# Revit family: Modelo mais complexo
name_source: partatom
category: Portas
revit_build: Autodesk Revit Architecture 2015 (Build: 20140606_1530(x64)
units: mm (PartAtom-declared; Revit-internal decimal feet)

## types (1)
- 2500 x 2100 mm
    Abertura º 2D = 45.00°
    Abertura º 3D = 45.00°
    Abertura º Auxiliar = 180.00°
    Altura = 2100
    Aro = Porta - Aro Pintura de Cor Branco
    Aro_Afastado Face Interior = 50  [stored 0.164042 ft]
    Aro_Espessura = 40  [stored 0.131234 ft]
    Batedor T = Porta - Batedor T Pintura de Cor Branco
    Comentários de tipos = 100% Paramétrico
    Couceira = Porta - Couceira Pintura de Cor Branco
    Couceira_Lateral = 125  [stored 0.410105 ft]
    Couceira_Travessa Inferior = 165  [stored 0.541339 ft]
    Couceira_Travessa Superior = 125  [stored 0.410105 ft]
    Descrição = Porta de Madeira - Mógno c/ Vidro Liso
    Fabricante = CESARITA
    Fechamento da parede = Por hospedeiro
    Fecho_Pano Exterior = 15  [stored 0.0492126 ft]
    Função = Interior
    Grosseiro = Porta - Grosseiro Pintura de Cor Branco
    Guarnição_Exterior = 5  [stored 0.0164042 ft]
    Guarnição_Interior = 15  [stored 0.0492126 ft]
    Largura = 3000  [stored 9.84252 ft]
    Modelo = 2 Folhas de Fole e 1 Folha de Abrir
    Moldura = Porta - Moldura
    Moldura_Espessura = 25  [stored 0.082021 ft]
    Moldura_Soleira Espessura = 45  [stored 0.147638 ft]
    Moldura_Travessa Lateral = 125  [stored 0.410105 ft]
    Moldura_Travessa Superior = 125  [stored 0.410105 ft]
    Painel_Espessura = 40  [stored 0.131234 ft]
    Painel_Largura = 1000  [stored 3.28084 ft]
    Puxador = Porta - Puxador
    Puxador_Altura = 500  [stored 1.64042 ft]
    Puxador_Distância X = 68
    Puxador_Distância Y = 1070  [stored 3.5105 ft]
    Soleira = Porta - Soleira
    Soleira_Espessura = 45  [stored 0.147638 ft]
    Soleira_Moldura Espessura = 25  [stored 0.082021 ft]
    Soleira_Ressalto = 45  [stored 0.147638 ft]
    Soleira_Ressalto Lateral = 30  [stored 0.0984252 ft]
    Travessa = Porta - Travessa Pintura de Cor Branco
    URL = www.cesarita.com
    Vidro = Porta - Vidro
    Visibilidade - Detalhe = Sim
    Visibilidade - Moldura = Sim
    Visibilidade - Paineis = Sim
    Vão_Altura = 2140
    Vão_Largura = 3080

note: [stored X ft] marks values corroborated as IEEE doubles in the binary element streams (Revit-internal decimal feet)

## geometry (parser evidence)
native form markers: Blend x44, Sweep x11
no freeform markers — native parametric forms only
